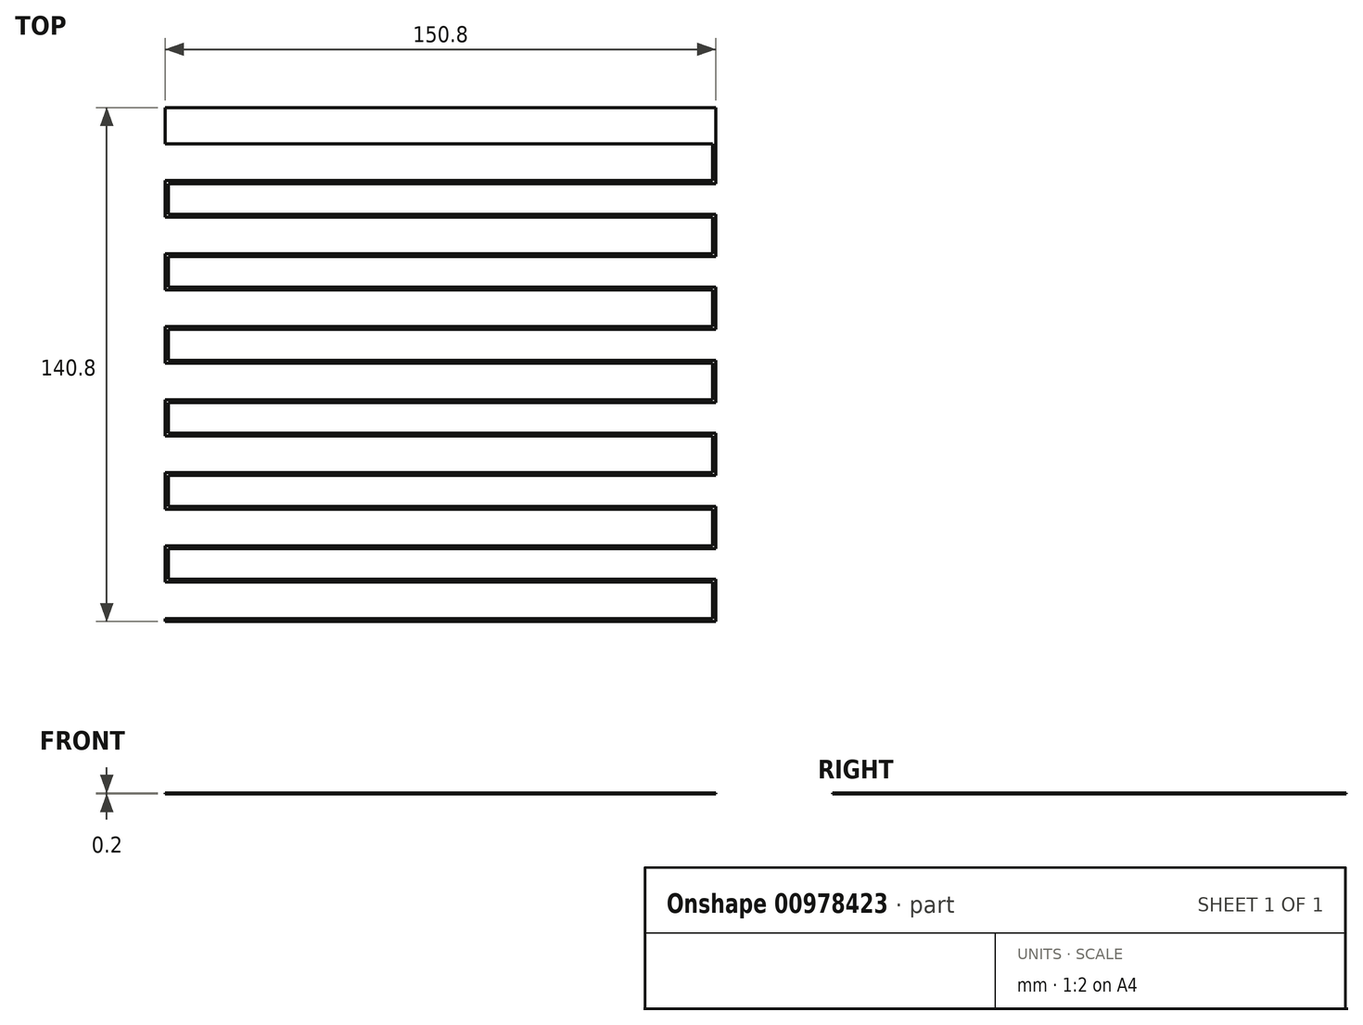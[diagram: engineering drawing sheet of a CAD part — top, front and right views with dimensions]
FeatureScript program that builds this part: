
annotation { "Feature Type Name" : "Feature", "Feature Type Description" : "" }
export const myFeature = defineFeature(function(context is Context, id is Id, definition is map)
    precondition{}
    {
        {
            var Q0;
            Q0=qCreatedBy(makeId("Top.planeOp"),FACE);
            var sketch = newSketch(context, id + "F0", { "sketchPlane" : qUnion([Q0])});
            skLineSegment(sketch, "E0", {"start": v(-75.14, -70) * mm, "end": v(74.86, -70) * mm});
            skLineSegment(sketch, "E1", {"start": v(74.86, -70) * mm, "end": v(74.86, -60) * mm});
            skLineSegment(sketch, "E2", {"start": v(74.86, -60) * mm, "end": v(-75.14, -60) * mm});
            skLineSegment(sketch, "E3", {"start": v(-75.14, -60) * mm, "end": v(-75.14, -50) * mm});
            skLineSegment(sketch, "E4", {"start": v(-75.14, -50) * mm, "end": v(74.86, -50) * mm});
            skLineSegment(sketch, "E5", {"start": v(74.86, -50) * mm, "end": v(74.86, -40) * mm});
            skLineSegment(sketch, "E6", {"start": v(74.86, -40) * mm, "end": v(-75.14, -40) * mm});
            skLineSegment(sketch, "E7", {"start": v(-75.14, -40) * mm, "end": v(-75.14, -30) * mm});
            skLineSegment(sketch, "E8", {"start": v(-75.14, -30) * mm, "end": v(74.86, -30) * mm});
            skLineSegment(sketch, "E9", {"start": v(74.86, -30) * mm, "end": v(74.86, -20) * mm});
            skLineSegment(sketch, "E10", {"start": v(74.86, -20) * mm, "end": v(-75.14, -20) * mm});
            skLineSegment(sketch, "E11", {"start": v(-75.14, -20) * mm, "end": v(-75.14, -10) * mm});
            skLineSegment(sketch, "E12", {"start": v(-75.14, -10) * mm, "end": v(74.86, -10) * mm});
            skLineSegment(sketch, "E13", {"start": v(74.86, -10) * mm, "end": v(74.86, 0) * mm});
            skLineSegment(sketch, "E14", {"start": v(74.86, 0) * mm, "end": v(-75.14, 0) * mm});
            skLineSegment(sketch, "E15", {"start": v(-75.14, 0) * mm, "end": v(-75.14, 10) * mm});
            skLineSegment(sketch, "E16", {"start": v(-75.14, 10) * mm, "end": v(74.86, 10) * mm});
            skLineSegment(sketch, "E17", {"start": v(74.86, 10) * mm, "end": v(74.86, 20) * mm});
            skLineSegment(sketch, "E18", {"start": v(74.86, 20) * mm, "end": v(-75.14, 20) * mm});
            skLineSegment(sketch, "E19", {"start": v(-75.14, 20) * mm, "end": v(-75.14, 30) * mm});
            skLineSegment(sketch, "E20", {"start": v(-75.14, 30) * mm, "end": v(74.86, 30) * mm});
            skPoint(sketch, "E20.endSnap0", {"position": v(74.86, 15) * mm});
            skLineSegment(sketch, "E21", {"start": v(74.86, 30) * mm, "end": v(74.86, 40) * mm});
            skLineSegment(sketch, "E22", {"start": v(74.86, 40) * mm, "end": v(-75.14, 40) * mm});
            skLineSegment(sketch, "E23", {"start": v(-75.14, 40) * mm, "end": v(-75.14, 50) * mm});
            skLineSegment(sketch, "E24", {"start": v(-75.14, 50) * mm, "end": v(74.86, 50) * mm});
            skLineSegment(sketch, "E25", {"start": v(74.86, 50) * mm, "end": v(74.86, 60) * mm});
            skLineSegment(sketch, "E26", {"start": v(74.86, 60) * mm, "end": v(-75.14, 60) * mm});
            skLineSegment(sketch, "E27", {"start": v(-75.14, 60) * mm, "end": v(-75.14, 70) * mm});
            skLineSegment(sketch, "E28", {"start": v(-75.14, 70) * mm, "end": v(75.66, 70) * mm});
            skLineSegment(sketch, "E29.3", {"start": v(75.66, 49.2) * mm, "end": v(75.66, 60.8) * mm});
            skLineSegment(sketch, "E29.4", {"start": v(-74.34, 49.2) * mm, "end": v(75.66, 49.2) * mm});
            skLineSegment(sketch, "E29.5", {"start": v(-74.34, 40.8) * mm, "end": v(-74.34, 49.2) * mm});
            skLineSegment(sketch, "E29.6", {"start": v(75.66, 40.8) * mm, "end": v(-74.34, 40.8) * mm});
            skLineSegment(sketch, "E29.7", {"start": v(75.66, -30.8) * mm, "end": v(75.66, -19.2) * mm});
            skLineSegment(sketch, "E29.8", {"start": v(-74.34, -30.8) * mm, "end": v(75.66, -30.8) * mm});
            skLineSegment(sketch, "E29.9", {"start": v(-74.34, -39.2) * mm, "end": v(-74.34, -30.8) * mm});
            skLineSegment(sketch, "E29.10", {"start": v(75.66, -39.2) * mm, "end": v(-74.34, -39.2) * mm});
            skLineSegment(sketch, "E29.11", {"start": v(75.66, -50.8) * mm, "end": v(75.66, -39.2) * mm});
            skLineSegment(sketch, "E29.12", {"start": v(-74.34, -50.8) * mm, "end": v(75.66, -50.8) * mm});
            skLineSegment(sketch, "E29.13", {"start": v(-75.14, -70.8) * mm, "end": v(75.66, -70.8) * mm});
            skLineSegment(sketch, "E29.14", {"start": v(75.66, -70.8) * mm, "end": v(75.66, -59.2) * mm});
            skLineSegment(sketch, "E29.15", {"start": v(75.66, -59.2) * mm, "end": v(-74.34, -59.2) * mm});
            skLineSegment(sketch, "E29.16", {"start": v(-74.34, -59.2) * mm, "end": v(-74.34, -50.8) * mm});
            skLineSegment(sketch, "E29.17", {"start": v(75.66, -19.2) * mm, "end": v(-74.34, -19.2) * mm});
            skLineSegment(sketch, "E29.18", {"start": v(-74.34, -19.2) * mm, "end": v(-74.34, -10.8) * mm});
            skLineSegment(sketch, "E29.19", {"start": v(-74.34, -10.8) * mm, "end": v(75.66, -10.8) * mm});
            skLineSegment(sketch, "E29.20", {"start": v(75.66, -10.8) * mm, "end": v(75.66, 0.8) * mm});
            skLineSegment(sketch, "E29.21", {"start": v(75.66, 0.8) * mm, "end": v(-74.34, 0.8) * mm});
            skLineSegment(sketch, "E29.22", {"start": v(-74.34, 0.8) * mm, "end": v(-74.34, 9.2) * mm});
            skLineSegment(sketch, "E29.23", {"start": v(-74.34, 9.2) * mm, "end": v(75.66, 9.2) * mm});
            skLineSegment(sketch, "E29.24", {"start": v(75.66, 9.2) * mm, "end": v(75.66, 20.8) * mm});
            skLineSegment(sketch, "E29.25", {"start": v(75.66, 20.8) * mm, "end": v(-74.34, 20.8) * mm});
            skLineSegment(sketch, "E29.26", {"start": v(-74.34, 20.8) * mm, "end": v(-74.34, 29.2) * mm});
            skLineSegment(sketch, "E29.27", {"start": v(-74.34, 29.2) * mm, "end": v(75.66, 29.2) * mm});
            skLineSegment(sketch, "E29.28", {"start": v(75.66, 29.2) * mm, "end": v(75.66, 40.8) * mm});
            skLineSegment(sketch, "E30", {"start": v(75.66, 70) * mm, "end": v(75.66, 69.2) * mm});
            skLineSegment(sketch, "E31", {"start": v(-75.14, -70) * mm, "end": v(-75.14, -70.8) * mm});
            skLineSegment(sketch, "E32", {"start": v(75.66, 69.2) * mm, "end": v(75.66, 60.8) * mm});
            skSolve(sketch);
        }
        {
            var Q0;
            Q0=makeQuery(id+"F0.imprint","IMPRINT",FACE,{"disambiguationData":[TD([[makeQuery(id+"F0.imprint","IMPRINT",EDGE,{"derivedFrom":sQuery(id+"F0.wireOp",EDGE,"E0")}),-1.0]])]});
            extrude(context, id + "F1", {"entities" : qUnion([Q0]), "flatOperationType" : FlatOperationType.REMOVE, "depth" : .2 * mm, "offsetDistance" : 25 * mm, "domain" : OperationDomain.MODEL});
        }
    });
